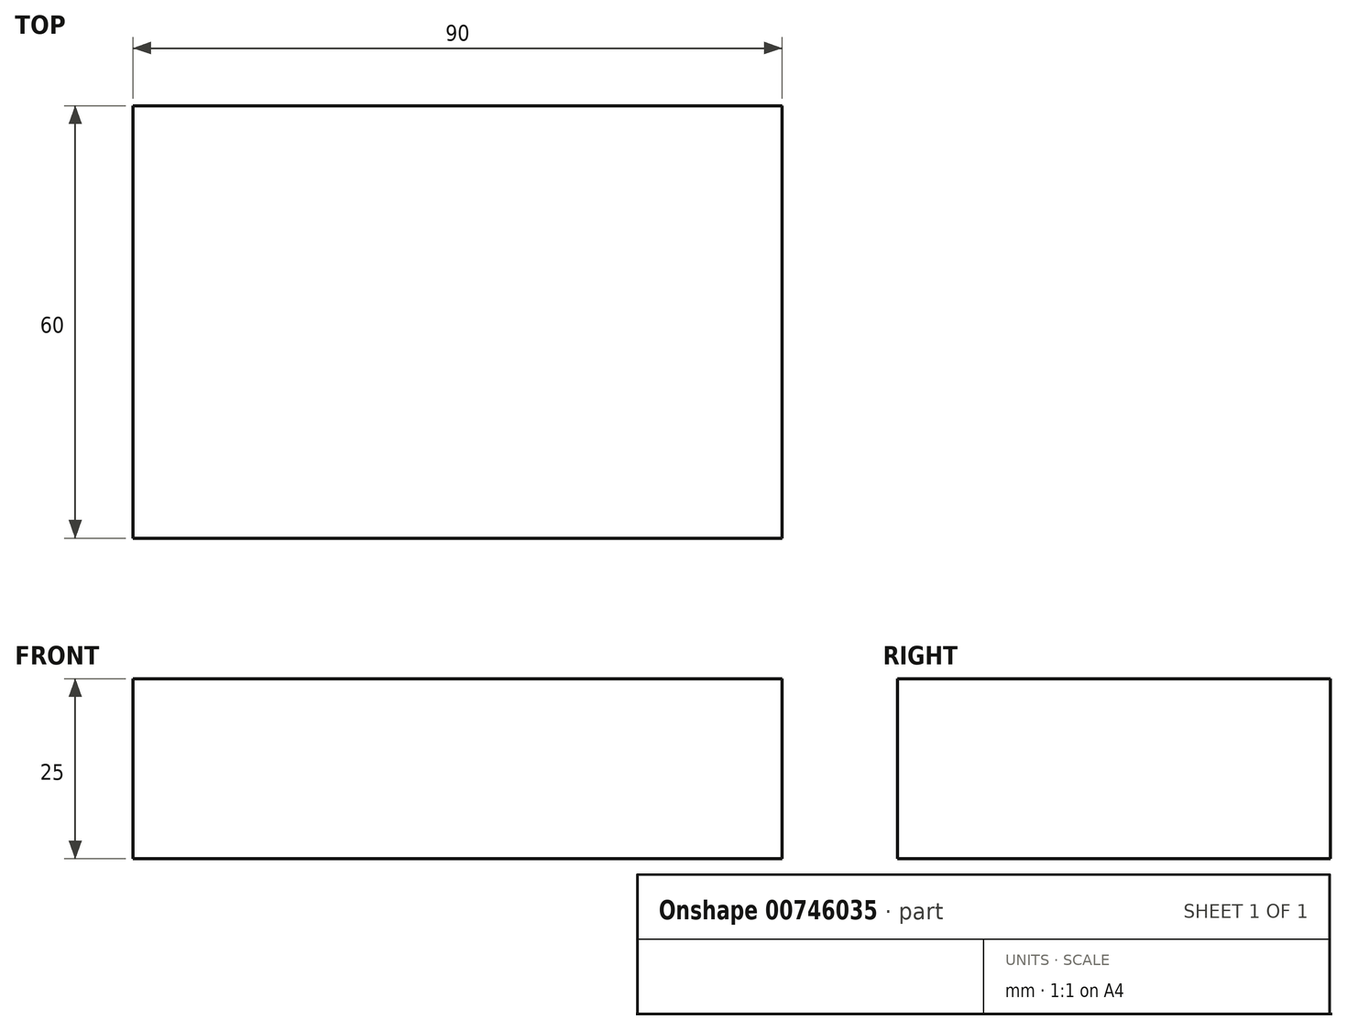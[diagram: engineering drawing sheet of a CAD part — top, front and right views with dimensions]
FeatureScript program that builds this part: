
annotation { "Feature Type Name" : "Feature", "Feature Type Description" : "" }
export const myFeature = defineFeature(function(context is Context, id is Id, definition is map)
    precondition{}
    {
        {
            var Q0;
            Q0=qCreatedBy(makeId("Top.planeOp"),FACE);
            var sketch = newSketch(context, id + "F0", { "sketchPlane" : qUnion([Q0])});
            skLineSegment(sketch, "E0.bottom", {"start": v(0, 0) * mm, "end": v(90, 0) * mm});
            skLineSegment(sketch, "E0.top", {"start": v(0, 60) * mm, "end": v(90, 60) * mm});
            skLineSegment(sketch, "E0.left", {"start": v(0, 0) * mm, "end": v(0, 60) * mm});
            skLineSegment(sketch, "E0.right", {"start": v(90, 0) * mm, "end": v(90, 60) * mm});
            skSolve(sketch);
        }
        {
            var Q0;
            Q0=makeQuery(id+"F0.imprint","IMPRINT",FACE,{"disambiguationData":[TD([[makeQuery(id+"F0.imprint","IMPRINT",EDGE,{"derivedFrom":sQuery(id+"F0.wireOp",EDGE,"E0.bottom")}),1.0]])]});
            extrude(context, id + "F1", {"entities" : qUnion([Q0]), "depth" : 25 * mm, "offsetDistance" : 25 * mm});
        }
    });
